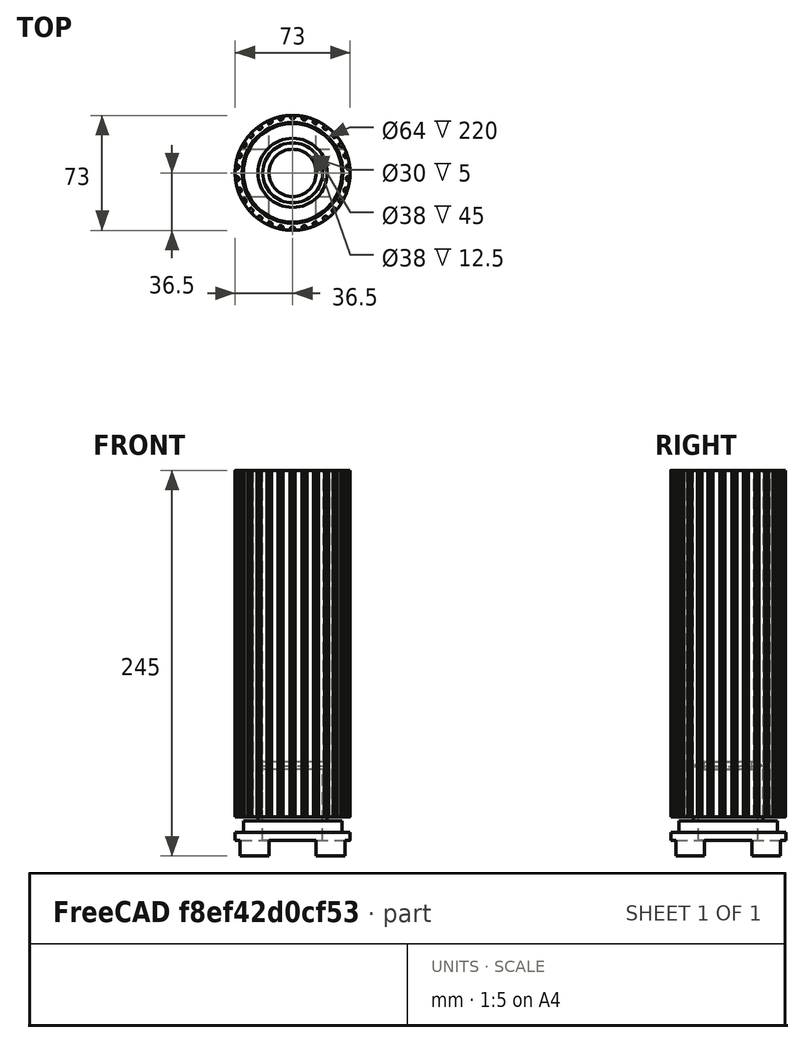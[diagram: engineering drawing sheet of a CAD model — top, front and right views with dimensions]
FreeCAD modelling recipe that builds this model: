
FCSTD DOCUMENT  (FreeCAD 0.15R4671 (Git))
Label: pica-small-v2
License: All rights reserved
LicenseURL: http://en.wikipedia.org/wiki/All_rights_reserved
objects: Drawing::FeatureView×10, Part::Cylinder×8, Part::Cut×7, Drawing::FeatureViewPart×6, Part::MultiFuse×5, Part::Box×4, Part::Part2DObjectPython×1, PartDesign::Pad×1, Drawing::FeaturePage×1, Part::Chamfer×1
note: 28 computed .brp shape members not serialized (recipe doc carries the construction recipe); baked Part::Feature solids carry a one-line shape summary decoded from their .brp

FEATURE [Part::Part2DObjectPython] InvoluteGear  # Draft 2D object (typed FeaturePython)
  ExternalGear = true
  HighPrecision = true
  Modules = 2.5
  NumberOfTeeth = 30
  PressureAngle = 20
FEATURE [PartDesign::Pad] Pad
  Length = 220
  Length2 = 100
  Sketch = -> InvoluteGear
  Type = 0
FEATURE [Part::Cylinder] Cylinder
  Angle = 360
  Height = 240
  Placement = pos=(0,0,-10) rot=(0,0,1;0rad)
  Radius = 32
FEATURE [Part::Cut] Cut  label="Final"
  Base = -> Pad
  Tool = -> Cylinder
FEATURE [Part::Cylinder] Cylinder001
  Angle = 360
  Height = 400
  Radius = 36.5
FEATURE [Part::Cylinder] Cylinder002
  Angle = 360
  Height = 400
  Radius = 100
FEATURE [Part::Cut] Cut001
  Base = -> Cylinder002
  Tool = -> Cylinder001
FEATURE [Part::Cut] Cut002  label="Shade"
  Base = -> Cut
  Placement = pos=(0,0,25) rot=(0,0,1;0rad)
  Tool = -> Cut001
FEATURE [Part::Cylinder] Cylinder003
  Angle = 360
  Height = 15
  Radius = 36.5
FEATURE [Part::Cylinder] Cylinder004
  Angle = 360
  Height = 22.5
  Radius = 31.3
FEATURE [Part::MultiFuse] Fusion  label="Base Fusion"
  Shapes = -> [Cylinder004,Cylinder003]
FEATURE [Part::Box] Box  label="Cube"
  Height = 10
  Length = 100
  Placement = pos=(-50,-15,0) rot=(0,0,1;0rad)
  Width = 30
FEATURE [Part::Box] Box001  label="Cube001"
  Height = 10
  Length = 100
  Placement = pos=(15,-50,0) rot=(0,0,1;1.5708rad)
  Width = 30
FEATURE [Part::MultiFuse] Fusion001  label="Feet Cutout Fusion"
  Shapes = -> [Box001,Box]
FEATURE [Drawing::FeatureViewPart] FrontView  label="Shade Side"
  Direction = (0,-1,0)
  HiddenWidth = 0.15
  LineWidth = 0.35
  Rotation = 90
  ShowHiddenLines = true
  ShowSmoothLines = false
  Source = -> Cut002
  Tolerance = 0.05
  ViewResult = <blob: 104580 chars omitted>
  Visible = true
  X = 80
  Y = 270
FEATURE [Drawing::FeatureViewPart] View001  label="Shade Top"
  Direction = (0,0,1)
  HiddenWidth = 0.15
  LineWidth = 0.35
  Rotation = 0
  ShowHiddenLines = false
  ShowSmoothLines = false
  Source = -> Cut002
  Tolerance = 0.05
  ViewResult = <blob: 17501 chars omitted>
  Visible = true
  X = 300
  Y = 80
FEATURE [Drawing::FeatureView] dim006  label="Base Radius"
  Rotation = 0
  ViewResult = <g   >\n <circle cx ="300.000000" cy ="170.000000" r="0.500000" stroke="none" fill="rgb(0,0,0)" /> \n<line x1="255.718312" y1="135.631286" x2="300.000000" y2="170.000000" style="stroke:rgb(0,0,0);stroke-width:0.30" />\n<polygon points="275.273643,150.808927 277.030448,153.438307 278.433561,153.261461 278.256715,151.858348" style="fill:rgb(0,0,0);stroke:rgb(0,0,0);stroke-width:0" />\n<line x1="255.718312" y1="135.631286" x2="231.639949" y2="135.631286" style="stroke:rgb(0,0,0);stroke-width:0.30" />\n<text x="219.448373" y="136.850443" font-family="Arial" font-size="3.6" fill="rgb(0,0,0)" text-anchor="inherit"  >R31.3</text>\n<!--31.3-->\n<!--R%3.3f-->\n</g> 
  Visible = true
  X = 0
  Y = 0
FEATURE [Drawing::FeatureView] centerLines
  Rotation = 0
  ViewResult = <g  transform="scale(1.000000,1.000000)" stroke="rgb(0,0,0)"  stroke-width="0.300000" >\n<path d="M 300.000000,170.000000 L 300.000000,168.000000 M 300.000000,166.000000 L 300.000000,160.000000 M 300.000000,158.000000 L 300.000000,156.000000 "/>\n<path d="M 300.000000,170.000000 L 302.000000,170.000000 M 304.000000,170.000000 L 310.000000,170.000000 M 312.000000,170.000000 L 314.000000,170.000000 "/>\n<path d="M 300.000000,170.000000 L 300.000000,172.000000 M 300.000000,174.000000 L 300.000000,180.000000 M 300.000000,182.000000 L 300.000000,184.000000 "/>\n<path d="M 300.000000,170.000000 L 298.000000,170.000000 M 296.000000,170.000000 L 290.000000,170.000000 M 288.000000,170.000000 L 286.000000,170.000000 "/>\n</g> 
  Visible = true
  X = 0
  Y = 0
FEATURE [Drawing::FeatureView] centerLines001
  Rotation = 0
  ViewResult = <g  transform="scale(1.000000,1.000000)" stroke="rgb(0,0,0)"  stroke-width="0.300000" >\n<path d="M 300.000000,80.000000 L 300.000000,82.000000 M 300.000000,84.000000 L 300.000000,90.000000 M 300.000000,92.000000 L 300.000000,94.000000 "/>\n<path d="M 300.000000,80.000000 L 302.000000,80.000000 M 304.000000,80.000000 L 310.000000,80.000000 M 312.000000,80.000000 L 314.000000,80.000000 "/>\n<path d="M 300.000000,80.000000 L 300.000000,78.000000 M 300.000000,76.000000 L 300.000000,70.000000 M 300.000000,68.000000 L 300.000000,66.000000 "/>\n<path d="M 300.000000,80.000000 L 298.000000,80.000000 M 296.000000,80.000000 L 290.000000,80.000000 M 288.000000,80.000000 L 286.000000,80.000000 "/>\n</g> 
  Visible = true
  X = 0
  Y = 0
FEATURE [Drawing::FeatureView] dim007  label="Shade Radius"
  Rotation = 0
  ViewResult = <g   >\n <circle cx ="300.000000" cy ="80.000000" r="0.500000" stroke="none" fill="rgb(0,0,0)" /> \n<line x1="340.917441" y1="111.884102" x2="300.000000" y2="80.000000" style="stroke:rgb(0,0,0);stroke-width:0.30" />\n<polygon points="325.241495,99.668933 323.489759,97.036174 322.086308,97.210316 322.260451,98.613767" style="fill:rgb(0,0,0);stroke:rgb(0,0,0);stroke-width:0" />\n<line x1="340.917441" y1="111.884102" x2="365.557939" y2="111.884102" style="stroke:rgb(0,0,0);stroke-width:0.30" />\n<text x="369.473360" y="112.835313" font-family="Arial" font-size="3.6" fill="rgb(0,0,0)" text-anchor="inherit"  >R32</text>\n<!--32.0-->\n<!--R%3.3f-->\n</g> 
  Visible = true
  X = 0
  Y = 0
FEATURE [Part::Cylinder] Cylinder005
  Angle = 360
  Height = 90
  Radius = 15
FEATURE [Part::Cylinder] Cylinder006
  Angle = 360
  Height = 55
  Radius = 19
FEATURE [Part::MultiFuse] Fusion002  label="Fixture Mount"
  Shapes = -> [Cylinder005,Cylinder006]
FEATURE [Drawing::FeatureViewPart] View004  label="Base Top"
  Direction = (0,0,1)
  HiddenWidth = 0.15
  LineWidth = 0.35
  Rotation = 0
  ShowHiddenLines = false
  ShowSmoothLines = false
  Tolerance = 0.05
  ViewResult = <g id="Base Top"\n   transform="rotate(0,300,170) translate(300,170) scale(1,1)"\n  >\n<g   stroke="rgb(0, 0, 0)"\n   stroke-width="0.35"\n   stroke-linecap="butt"\n   stroke-linejoin="miter"\n   fill="none"\n   transform="scale(1,-1)"\n  >\n<circle cx ="0" cy ="0" r ="23.3" /><circle cx ="0" cy ="0" r ="15" /><circle cx ="0" cy ="0" r ="31.3" /><circle cx ="0" cy ="0" r ="36.5" /></g>\n</g>
  Visible = true
  X = 300
  Y = 170
FEATURE [Drawing::FeatureViewPart] View005  label="Base Side"
  Direction = (0,-1,0)
  HiddenWidth = 0.15
  LineWidth = 0.35
  Rotation = 90
  ShowHiddenLines = false
  ShowSmoothLines = false
  Tolerance = 0.05
  ViewResult = <blob: 2600 chars omitted>
  Visible = true
  X = 80
  Y = 270
FEATURE [Drawing::FeatureViewPart] View  label="Base Side001"
  Direction = (0,-1,0)
  HiddenWidth = 0.15
  LineWidth = 0.35
  Rotation = 90
  ShowHiddenLines = false
  ShowSmoothLines = false
  Tolerance = 0.05
  ViewResult = <blob: 2605 chars omitted>
  Visible = true
  X = 180
  Y = 100
FEATURE [Drawing::FeatureViewPart] View006  label="Base Top001"
  Direction = (0,0,-1)
  HiddenWidth = 0.15
  LineWidth = 0.35
  Rotation = 0
  ShowHiddenLines = false
  ShowSmoothLines = false
  Tolerance = 0.05
  ViewResult = <blob: 2659 chars omitted>
  Visible = true
  X = 180
  Y = 170
FEATURE [Drawing::FeatureView] dim010  label="dim001"
  Rotation = 0
  ViewResult = <g   >\n<line x1="158.500000" y1="235.000000" x2="177.679727" y2="235.000000" style="stroke:rgb(0,0,0);stroke-width:0.30" />\n<line x1="158.483300" y1="250.000000" x2="177.679727" y2="250.000000" style="stroke:rgb(0,0,0);stroke-width:0.30" />\n<line x1="176.679727" y1="235.000000" x2="176.679727" y2="250.000000" style="stroke:rgb(0,0,0);stroke-width:0.30" />\n<polygon points="176.679727,235.000000 175.679727,238.000000 176.679727,239.000000 177.679727,238.000000" style="fill:rgb(0,0,0);stroke:rgb(0,0,0);stroke-width:0" /><polygon points="176.679727,250.000000 177.679727,247.000000 176.679727,246.000000 175.679727,247.000000" style="fill:rgb(0,0,0);stroke:rgb(0,0,0);stroke-width:0" />\n<text x="183.587709" y="244.783611" font-family="Arial" font-size="3.6" fill="rgb(0,0,0)" text-anchor="inherit" transform="rotate(-90.000000 183.587709,244.783611)" >15</text>\n</g> 
  Visible = true
  X = 0
  Y = 0
FEATURE [Drawing::FeatureView] dim011  label="dim002"
  Rotation = 0
  ViewResult = <g   >\n<line x1="153.300000" y1="228.000000" x2="177.810311" y2="228.000000" style="stroke:rgb(0,0,0);stroke-width:0.30" />\n<line x1="158.500000" y1="235.000000" x2="177.810311" y2="235.000000" style="stroke:rgb(0,0,0);stroke-width:0.30" />\n<line x1="176.810311" y1="228.000000" x2="176.810311" y2="235.000000" style="stroke:rgb(0,0,0);stroke-width:0.30" />\n<polygon points="176.810311,228.000000 177.810311,225.000000 176.810311,224.000000 175.810311,225.000000" style="fill:rgb(0,0,0);stroke:rgb(0,0,0);stroke-width:0" /><polygon points="176.810311,235.000000 175.810311,238.000000 176.810311,239.000000 177.810311,238.000000" style="fill:rgb(0,0,0);stroke:rgb(0,0,0);stroke-width:0" />\n<text x="183.208911" y="232.569545" font-family="Arial" font-size="3.6" fill="rgb(0,0,0)" text-anchor="inherit" transform="rotate(-90.000000 183.208911,232.569545)" >7</text>\n</g> 
  Visible = true
  X = 0
  Y = 0
FEATURE [Drawing::FeatureView] centerLines004
  Rotation = 0
  ViewResult = <g  transform="scale(1.000000,1.000000)" stroke="rgb(0,0,0)"  stroke-width="0.300000" >\n<path d="M 180.000000,169.999925 L 180.000000,167.999925 M 180.000000,165.999925 L 180.000000,159.999925 M 180.000000,157.999925 L 180.000000,155.999925 "/>\n<path d="M 180.000000,169.999925 L 182.000000,169.999925 M 184.000000,169.999925 L 190.000000,169.999925 M 192.000000,169.999925 L 194.000000,169.999925 "/>\n<path d="M 180.000000,169.999925 L 180.000000,171.999925 M 180.000000,173.999925 L 180.000000,179.999925 M 180.000000,181.999925 L 180.000000,183.999925 M 180.000000,185.999925 L 180.000000,186.160469 "/>\n<path d="M 180.000000,169.999925 L 178.000000,169.999925 M 176.000000,169.999925 L 170.000000,169.999925 M 168.000000,169.999925 L 166.583365,169.999925 "/>\n</g> 
  Visible = true
  X = 0
  Y = 0
FEATURE [Drawing::FeatureView] dim
  Rotation = 0
  ViewResult = <g   >\n<line x1="41.500000" y1="25.000000" x2="33.944194" y2="25.000000" style="stroke:rgb(0,0,0);stroke-width:0.30" />\n<line x1="41.500000" y1="245.000000" x2="33.944194" y2="245.000000" style="stroke:rgb(0,0,0);stroke-width:0.30" />\n<line x1="34.944194" y1="25.000000" x2="34.944194" y2="245.000000" style="stroke:rgb(0,0,0);stroke-width:0.30" />\n<polygon points="34.944194,25.000000 33.944194,28.000000 34.944194,29.000000 35.944194,28.000000" style="fill:rgb(0,0,0);stroke:rgb(0,0,0);stroke-width:0" /><polygon points="34.944194,245.000000 35.944194,242.000000 34.944194,241.000000 33.944194,242.000000" style="fill:rgb(0,0,0);stroke:rgb(0,0,0);stroke-width:0" />\n<text x="31.608126" y="136.256650" font-family="Arial" font-size="3.6" fill="rgb(0,0,0)" text-anchor="inherit" transform="rotate(-90.000000 31.608126,136.256650)" >220</text>\n</g> 
  Visible = true
  X = 0
  Y = 0
FEATURE [Drawing::FeatureView] dim012
  Rotation = 0
  ViewResult = <g   >\n<line x1="118.122400" y1="245.000000" x2="126.861722" y2="245.000000" style="stroke:rgb(0,0,0);stroke-width:0.30" />\n<line x1="115.275400" y1="270.000000" x2="126.861722" y2="270.000000" style="stroke:rgb(0,0,0);stroke-width:0.30" />\n<line x1="125.861722" y1="245.000000" x2="125.861722" y2="270.000000" style="stroke:rgb(0,0,0);stroke-width:0.30" />\n<polygon points="125.861722,245.000000 124.861722,248.000000 125.861722,249.000000 126.861722,248.000000" style="fill:rgb(0,0,0);stroke:rgb(0,0,0);stroke-width:0" /><polygon points="125.861722,270.000000 126.861722,267.000000 125.861722,266.000000 124.861722,267.000000" style="fill:rgb(0,0,0);stroke:rgb(0,0,0);stroke-width:0" />\n<text x="132.056471" y="260.197520" font-family="Arial" font-size="3.6" fill="rgb(0,0,0)" text-anchor="inherit" transform="rotate(-90.000000 132.056471,260.197520)" >25</text>\n</g> 
  Visible = true
  X = 0
  Y = 0
FEATURE [Drawing::FeatureView] dim013
  Rotation = 0
  ViewResult = <g   >\n<line x1="143.500000" y1="73.000000" x2="143.500000" y2="45.465562" style="stroke:rgb(0,0,0);stroke-width:0.30" />\n<line x1="216.500000" y1="73.000000" x2="216.500000" y2="45.465562" style="stroke:rgb(0,0,0);stroke-width:0.30" />\n<line x1="143.500000" y1="46.465562" x2="216.500000" y2="46.465562" style="stroke:rgb(0,0,0);stroke-width:0.30" />\n<polygon points="143.500000,46.465562 146.500000,47.465562 147.500000,46.465562 146.500000,45.465562" style="fill:rgb(0,0,0);stroke:rgb(0,0,0);stroke-width:0" /><polygon points="216.500000,46.465562 213.500000,45.465562 212.500000,46.465562 213.500000,47.465562" style="fill:rgb(0,0,0);stroke:rgb(0,0,0);stroke-width:0" />\n<text x="177.413963" y="43.541156" font-family="Arial" font-size="3.6" fill="rgb(0,0,0)" text-anchor="inherit" transform="rotate(0.000000 177.413963,43.541156)" >73</text>\n</g> 
  Visible = true
  X = 0
  Y = 0
FEATURE [Drawing::FeaturePage] AutoDrawing  label="Initial Sketch"
  EditableTexts = FLOYD DIEBEL | 8/22/2015 | 1:1 | 1 | 1 | PICA (SMALL V2) | LAMP WITH SHADE
  Group = -> [FrontView,View001,dim006,centerLines,centerLines001,dim007,View004,View005,dim010,dim011,View,View006,centerLines004,dim,dim012,dim013]
  Template = C:/Program Files/FreeCAD 0.15/data/Mod/Drawing/Templates/A3_Landscape.svg
FEATURE [Part::Cylinder] Cylinder007
  Angle = 360
  Height = 60
  Radius = 22
FEATURE [Part::MultiFuse] Fusion003
  Shapes = -> [Fusion,Cylinder007]
FEATURE [Part::Cut] Cut005  label="Raw"
  Base = -> Fusion003
  Tool = -> Fusion002
FEATURE [Part::Cut] Cut003  label="Plain Base"
  Base = -> Fusion
  Tool = -> Fusion001
FEATURE [Part::Cut] Cut004  label="Base w/ Mount"
  Base = -> Cut003
  Tool = -> Fusion002
FEATURE [Part::Box] Box002  label="Cube002"
  Height = 10
  Length = 100
  Placement = pos=(-50,-15,0) rot=(0,0,1;0rad)
  Width = 30
FEATURE [Part::Box] Box003  label="Cube003"
  Height = 10
  Length = 100
  Placement = pos=(15,-50,0) rot=(0,0,1;1.5708rad)
  Width = 30
FEATURE [Part::MultiFuse] Fusion004  label="Feet Cutout Fusion001"
  Shapes = -> [Box003,Box002]
FEATURE [Part::Cut] Cut006  label="Pre-chamfer"
  Base = -> Cut005
  Tool = -> Fusion004
FEATURE [Part::Chamfer] Chamfer
  Base = -> Cut006
  Edges = 1 edges r=3: [Edge1]
